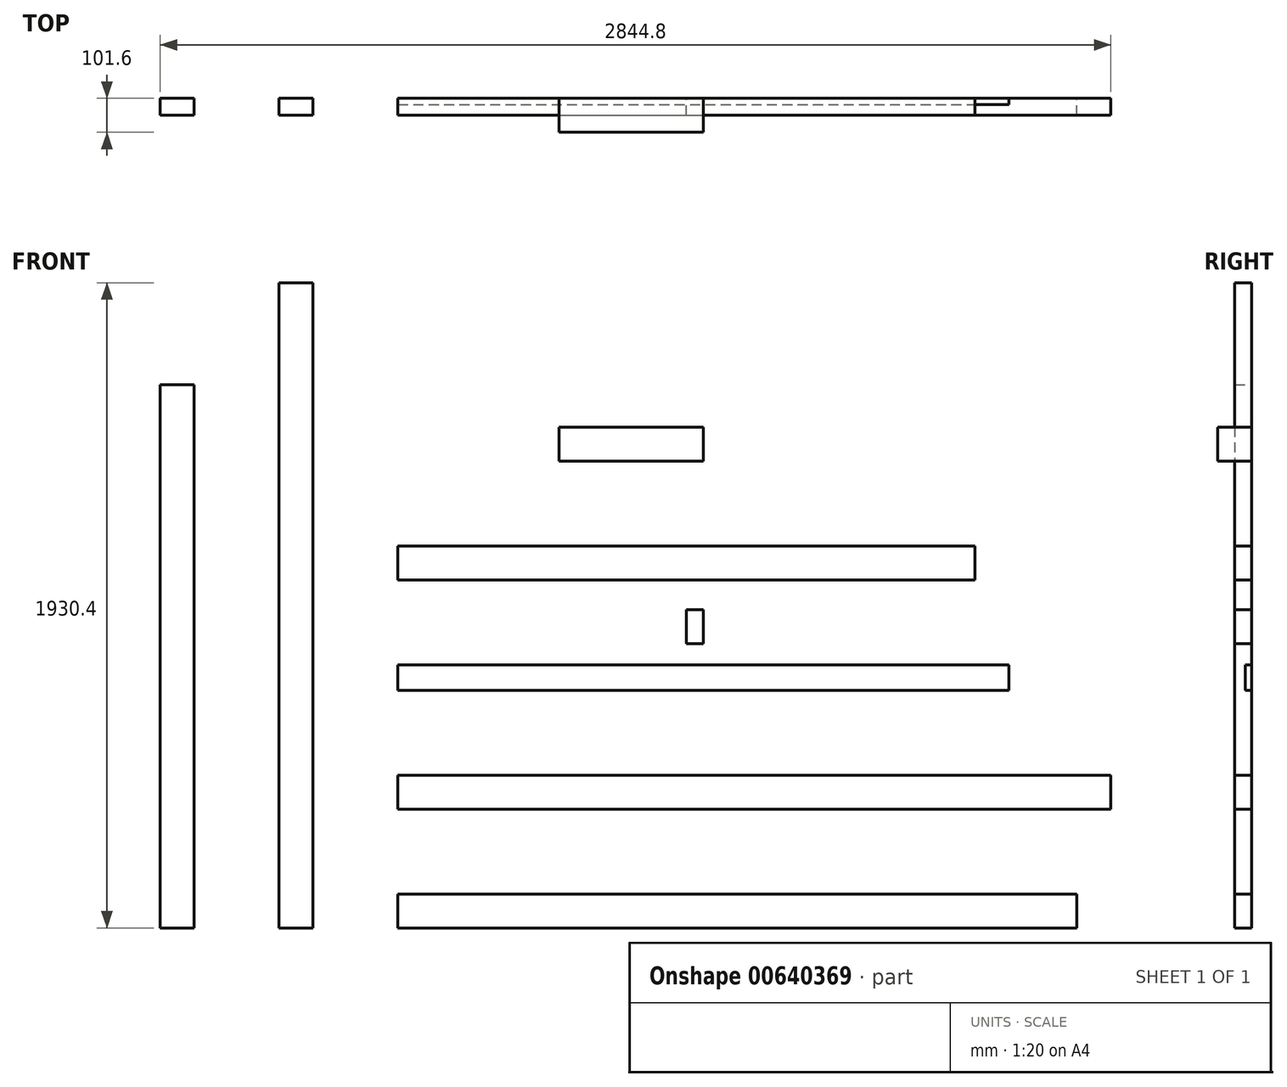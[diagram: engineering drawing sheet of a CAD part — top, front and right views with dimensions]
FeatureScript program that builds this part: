
annotation { "Feature Type Name" : "Feature", "Feature Type Description" : "" }
export const myFeature = defineFeature(function(context is Context, id is Id, definition is map)
    precondition{}
    {
        {
            assignVariable(context, id + "F0", {"name" : "SupportWood_Thickness", "anyValue" : 50.8 * mm});
        }
        {
            assignVariable(context, id + "F1", {"name" : "PlatformSlate_Thickness", "anyValue" : 19.05 * mm});
        }
        {
            var Q0;
            Q0=qCreatedBy(makeId("Front.planeOp"),FACE);
            var sketch = newSketch(context, id + "F2", { "sketchPlane" : qUnion([Q0])});
            skLineSegment(sketch, "E0.bottom", {"start": v(-914.4, 38.1) * mm, "end": v(914.4, 38.1) * mm});
            skLineSegment(sketch, "E0.top", {"start": v(-914.4, -38.1) * mm, "end": v(914.4, -38.1) * mm});
            skLineSegment(sketch, "E0.left", {"start": v(-914.4, 38.1) * mm, "end": v(-914.4, -38.1) * mm});
            skLineSegment(sketch, "E0.right", {"start": v(914.4, 38.1) * mm, "end": v(914.4, -38.1) * mm});
            skLineSegment(sketch, "E1", {"start": v(-914.4, 38.1) * mm, "end": v(914.4, -38.1) * mm, "construction": true});
            skLineSegment(sketch, "E2", {"start": v(914.4, 38.1) * mm, "end": v(-914.4, -38.1) * mm, "construction": true});
            skSolve(sketch);
        }
        {
            var Q0;
            Q0 = qSketchRegion(id + "F2", true);
            extrude(context, id + "F3", {"entities" : qUnion([Q0]), "depth" : getVariable(context, 'PlatformSlate_Thickness'), "offsetDistance" : 25.4 * mm});
        }
        {
            var Q0;
            Q0=qCreatedBy(makeId("Front.planeOp"),FACE);
            var sketch = newSketch(context, id + "F4", { "sketchPlane" : qUnion([Q0])});
            skLineSegment(sketch, "E3.bottom", {"start": v(-914.4, -292.1) * mm, "end": v(1219.2, -292.1) * mm});
            skLineSegment(sketch, "E3.top", {"start": v(-914.4, -393.7) * mm, "end": v(1219.2, -393.7) * mm});
            skLineSegment(sketch, "E3.left", {"start": v(-914.4, -292.1) * mm, "end": v(-914.4, -393.7) * mm});
            skLineSegment(sketch, "E3.right", {"start": v(1219.2, -292.1) * mm, "end": v(1219.2, -393.7) * mm});
            skSolve(sketch);
        }
        {
            var Q0;
            Q0=makeQuery(id+"F4.imprint","IMPRINT",FACE,{"disambiguationData":[TD([[makeQuery(id+"F4.imprint","IMPRINT",EDGE,{"derivedFrom":sQuery(id+"F4.wireOp",EDGE,"E3.bottom")}),-1.0]])]});
            extrude(context, id + "F5", {"entities" : qUnion([Q0]), "depth" : getVariable(context, 'SupportWood_Thickness'), "offsetDistance" : 25.4 * mm});
        }
        {
            var Q0;
            Q0=qCreatedBy(makeId("Front.planeOp"),FACE);
            var sketch = newSketch(context, id + "F6", { "sketchPlane" : qUnion([Q0])});
            skLineSegment(sketch, "E4.bottom", {"start": v(-914.4, -647.7) * mm, "end": v(1117.6, -647.7) * mm});
            skLineSegment(sketch, "E4.top", {"start": v(-914.4, -749.3) * mm, "end": v(1117.6, -749.3) * mm});
            skLineSegment(sketch, "E4.left", {"start": v(-914.4, -647.7) * mm, "end": v(-914.4, -749.3) * mm});
            skLineSegment(sketch, "E4.right", {"start": v(1117.6, -647.7) * mm, "end": v(1117.6, -749.3) * mm});
            skSolve(sketch);
        }
        {
            var Q0;
            Q0=makeQuery(id+"F6.imprint","IMPRINT",FACE,{"disambiguationData":[TD([[makeQuery(id+"F6.imprint","IMPRINT",EDGE,{"derivedFrom":sQuery(id+"F6.wireOp",EDGE,"E4.bottom")}),-1.0]])]});
            extrude(context, id + "F7", {"entities" : qUnion([Q0]), "depth" : getVariable(context, 'SupportWood_Thickness'), "offsetDistance" : 25.4 * mm});
        }
        {
            var Q0;
            Q0=qCreatedBy(makeId("Front.planeOp"),FACE);
            var sketch = newSketch(context, id + "F8", { "sketchPlane" : qUnion([Q0])});
            skLineSegment(sketch, "E5.bottom", {"start": v(-914.4, 292.1) * mm, "end": v(812.8, 292.1) * mm});
            skLineSegment(sketch, "E5.top", {"start": v(-914.4, 393.7) * mm, "end": v(812.8, 393.7) * mm});
            skLineSegment(sketch, "E5.left", {"start": v(-914.4, 292.1) * mm, "end": v(-914.4, 393.7) * mm});
            skLineSegment(sketch, "E5.right", {"start": v(812.8, 292.1) * mm, "end": v(812.8, 393.7) * mm});
            skSolve(sketch);
        }
        {
            var Q0;
            Q0=makeQuery(id+"F8.imprint","IMPRINT",FACE,{"disambiguationData":[TD([[makeQuery(id+"F8.imprint","IMPRINT",EDGE,{"derivedFrom":sQuery(id+"F8.wireOp",EDGE,"E5.bottom")}),1.0]])]});
            extrude(context, id + "F9", {"entities" : qUnion([Q0]), "depth" : getVariable(context, 'SupportWood_Thickness'), "offsetDistance" : 25.4 * mm});
        }
        {
            var Q0;
            Q0=qCreatedBy(makeId("Front.planeOp"),FACE);
            var sketch = newSketch(context, id + "F10", { "sketchPlane" : qUnion([Q0])});
            skLineSegment(sketch, "E6.bottom", {"start": v(-50.8, 203.2) * mm, "end": v(0, 203.2) * mm});
            skLineSegment(sketch, "E6.top", {"start": v(-50.8, 101.6) * mm, "end": v(0, 101.6) * mm});
            skLineSegment(sketch, "E6.left", {"start": v(-50.8, 203.2) * mm, "end": v(-50.8, 101.6) * mm});
            skLineSegment(sketch, "E6.right", {"start": v(0, 203.2) * mm, "end": v(0, 101.6) * mm});
            skSolve(sketch);
        }
        {
            var Q0;
            Q0 = qSketchRegion(id + "F10", true);
            extrude(context, id + "F11", {"entities" : qUnion([Q0]), "depth" : 50.8 * mm, "offsetDistance" : 25.4 * mm});
        }
        {
            var Q0;
            Q0=qCreatedBy(makeId("Front.planeOp"),FACE);
            var sketch = newSketch(context, id + "F12", { "sketchPlane" : qUnion([Q0])});
            skLineSegment(sketch, "E7.bottom", {"start": v(0, 647.7) * mm, "end": v(-431.8, 647.7) * mm});
            skLineSegment(sketch, "E7.top", {"start": v(0, 749.3) * mm, "end": v(-431.8, 749.3) * mm});
            skLineSegment(sketch, "E7.left", {"start": v(0, 647.7) * mm, "end": v(0, 749.3) * mm});
            skLineSegment(sketch, "E7.right", {"start": v(-431.8, 647.7) * mm, "end": v(-431.8, 749.3) * mm});
            skSolve(sketch);
        }
        {
            var Q0;
            Q0 = qSketchRegion(id + "F12", true);
            extrude(context, id + "F13", {"entities" : qUnion([Q0]), "depth" : 101.6 * mm, "offsetDistance" : 25.4 * mm});
        }
        {
            var Q0;
            Q0=qCreatedBy(makeId("Front.planeOp"),FACE);
            var sketch = newSketch(context, id + "F14", { "sketchPlane" : qUnion([Q0])});
            skLineSegment(sketch, "E8.bottom", {"start": v(-1168.4, 1181.1) * mm, "end": v(-1270, 1181.1) * mm});
            skLineSegment(sketch, "E8.top", {"start": v(-1168.4, -749.3) * mm, "end": v(-1270, -749.3) * mm});
            skLineSegment(sketch, "E8.left", {"start": v(-1168.4, 1181.1) * mm, "end": v(-1168.4, -749.3) * mm});
            skLineSegment(sketch, "E8.right", {"start": v(-1270, 1181.1) * mm, "end": v(-1270, -749.3) * mm});
            skSolve(sketch);
        }
        {
            var Q0;
            Q0=makeQuery(id+"F14.imprint","IMPRINT",FACE,{"disambiguationData":[TD([[makeQuery(id+"F14.imprint","IMPRINT",EDGE,{"derivedFrom":sQuery(id+"F14.wireOp",EDGE,"E8.bottom")}),1.0]])]});
            extrude(context, id + "F15", {"entities" : qUnion([Q0]), "depth" : 50.8 * mm, "offsetDistance" : 25.4 * mm});
        }
        {
            var Q0;
            Q0=qCreatedBy(makeId("Front.planeOp"),FACE);
            var sketch = newSketch(context, id + "F16", { "sketchPlane" : qUnion([Q0])});
            skLineSegment(sketch, "E9.bottom", {"start": v(-1524, 876.3) * mm, "end": v(-1625.6, 876.3) * mm});
            skLineSegment(sketch, "E9.top", {"start": v(-1524, -749.3) * mm, "end": v(-1625.6, -749.3) * mm});
            skLineSegment(sketch, "E9.left", {"start": v(-1524, 876.3) * mm, "end": v(-1524, -749.3) * mm});
            skLineSegment(sketch, "E9.right", {"start": v(-1625.6, 876.3) * mm, "end": v(-1625.6, -749.3) * mm});
            skSolve(sketch);
        }
        {
            var Q0;
            Q0 = qSketchRegion(id + "F16", true);
            extrude(context, id + "F17", {"entities" : qUnion([Q0]), "depth" : 50.8 * mm, "offsetDistance" : 25.4 * mm});
        }
    });
